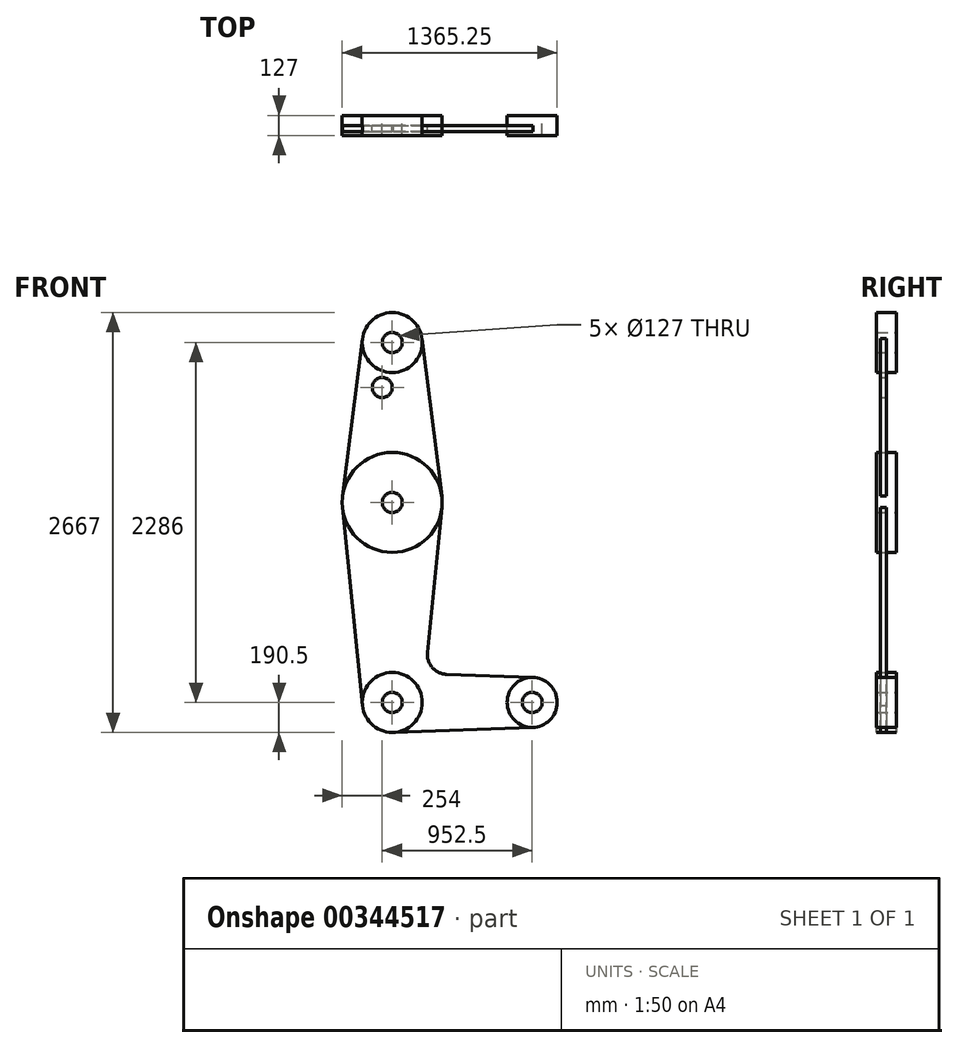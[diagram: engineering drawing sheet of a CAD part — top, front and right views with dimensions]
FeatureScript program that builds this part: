
annotation { "Feature Type Name" : "Feature", "Feature Type Description" : "" }
export const myFeature = defineFeature(function(context is Context, id is Id, definition is map)
    precondition{}
    {
        {
            var Q0;
            Q0=qCreatedBy(makeId("Front.planeOp"),FACE);
            var sketch = newSketch(context, id + "F0", { "sketchPlane" : qUnion([Q0])});
            skLineSegment(sketch, "E0", {"start": v(0, 2286) * mm, "end": v(0, 0) * mm, "construction": true});
            skLineSegment(sketch, "E1", {"start": v(0, 0) * mm, "end": v(889, 0) * mm, "construction": true});
            skCircle(sketch, "E2", {"center": v(0, 2286) * mm, "radius": 190.5 * mm});
            skCircle(sketch, "E3", {"center": v(0, 1270) * mm, "radius": 317.5 * mm});
            skCircle(sketch, "E4", {"center": v(0, 0) * mm, "radius": 190.5 * mm});
            skCircle(sketch, "E5", {"center": v(889, 0) * mm, "radius": 158.75 * mm});
            skLineSegment(sketch, "E6", {"start": v(-189, 2309.81) * mm, "end": v(-315, 1309.69) * mm});
            skLineSegment(sketch, "E7", {"start": v(189, 2309.81) * mm, "end": v(315, 1309.69) * mm});
            skCircle(sketch, "E8", {"center": v(0, 2286) * mm, "radius": 63.5 * mm});
            skCircle(sketch, "E9", {"center": v(0, 1270) * mm, "radius": 63.5 * mm});
            skCircle(sketch, "E10", {"center": v(0, 0) * mm, "radius": 63.5 * mm});
            skCircle(sketch, "E11", {"center": v(889, 0) * mm, "radius": 63.5 * mm});
            skPoint(sketch, "E12", {"position": v(-63.5, 2000.25) * mm});
            skCircle(sketch, "E13", {"center": v(-63.5, 2000.25) * mm, "radius": 63.5 * mm});
            skLineSegment(sketch, "E14", {"start": v(315.9, 1238.25) * mm, "end": v(223.41, 317.9) * mm});
            skLineSegment(sketch, "E15", {"start": v(6.8, -190.38) * mm, "end": v(894.67, -158.65) * mm});
            skLineSegment(sketch, "E16", {"start": v(345.24, 178.28) * mm, "end": v(894.67, 158.65) * mm});
            skLineSegment(sketch, "E17", {"start": v(-315.9, 1238.25) * mm, "end": v(-189.55, -19.05) * mm});
            skArc(sketch, "E18.filletArc", {"start": v(223.41, 317.9) * mm, "mid": v(254.08, 221.7) * mm, "end": v(345.24, 178.28) * mm});
            skSolve(sketch);
        }
        {
            var Q0;
            Q0=makeQuery(id+"F0.imprint","IMPRINT",FACE,{"disambiguationData":[TD([[makeQuery(id+"F0.imprint","IMPRINT",EDGE,{"derivedFrom":sQuery(id+"F0.wireOp",EDGE,"E8")}),-1.0]])]});
            var Q1;
            Q1=makeQuery(id+"F0.imprint","IMPRINT",FACE,{"disambiguationData":[TD([[makeQuery(id+"F0.imprint","IMPRINT",EDGE,{"derivedFrom":sQuery(id+"F0.wireOp",EDGE,"E9")}),-1.0]])]});
            var Q2;
            Q2=makeQuery(id+"F0.imprint","IMPRINT",FACE,{"disambiguationData":[TD([[makeQuery(id+"F0.imprint","IMPRINT",EDGE,{"derivedFrom":sQuery(id+"F0.wireOp",EDGE,"E10")}),-1.0]])]});
            var Q3;
            Q3=makeQuery(id+"F0.imprint","IMPRINT",FACE,{"disambiguationData":[TD([[makeQuery(id+"F0.imprint","IMPRINT",EDGE,{"derivedFrom":sQuery(id+"F0.wireOp",EDGE,"E11")}),-1.0]])]});
            extrude(context, id + "F1", {"entities" : qUnion([Q0, Q1, Q2, Q3]), "endBound" : BoundingType.SYMMETRIC, "depth" : 127 * mm});
        }
        {
            var Q0;
            {var subQ0=sQuery(id+"F0.wireOp",EDGE,"E6");Q0=makeQuery(id+"F0.imprint","IMPRINT",FACE,{"disambiguationData":[TD([[makeQuery(id+"F0.imprint","IMPRINT",EDGE,{"derivedFrom":subQ0}),1.0]])]});}
            var Q1;
            {var subQ3=sQuery(id+"F0.wireOp",EDGE,"E14");Q1=makeQuery(id+"F0.imprint","IMPRINT",FACE,{"disambiguationData":[TD([[makeQuery(id+"F0.imprint","IMPRINT",EDGE,{"derivedFrom":subQ3}),-1.0]])]});}
            extrude(context, id + "F2", {"entities" : qUnion([Q0, Q1]), "depth" : 38.1 * mm});
        }
    });
